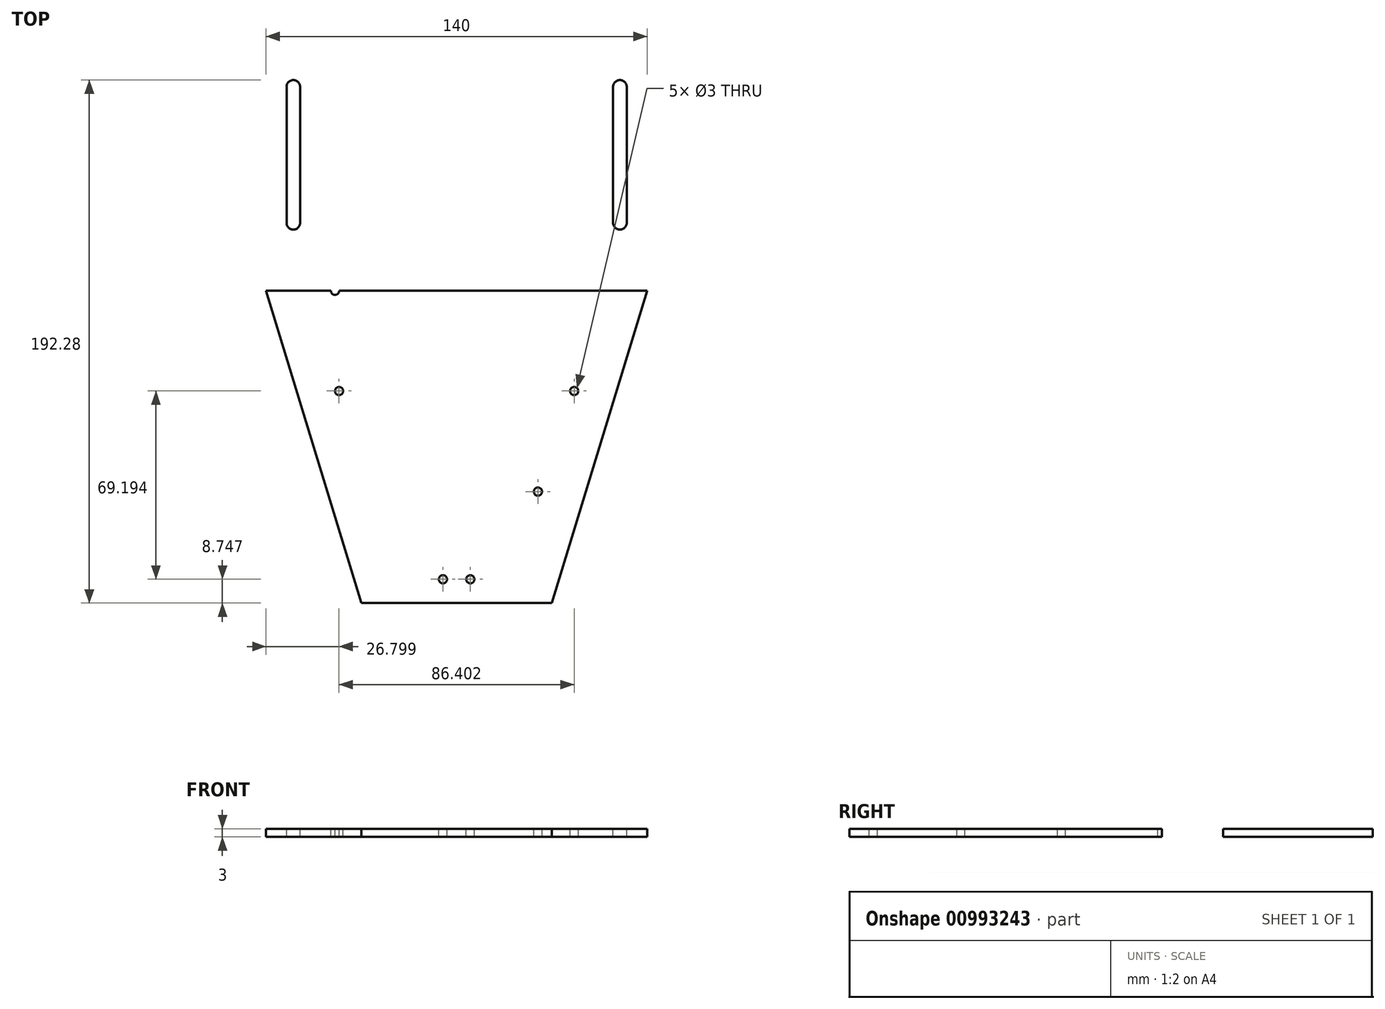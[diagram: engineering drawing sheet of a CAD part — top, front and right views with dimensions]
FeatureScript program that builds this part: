
annotation { "Feature Type Name" : "Feature", "Feature Type Description" : "" }
export const myFeature = defineFeature(function(context is Context, id is Id, definition is map)
    precondition{}
    {
        {
            var Q0;
            Q0=qCreatedBy(makeId("Top.planeOp"),FACE);
            var sketch = newSketch(context, id + "F0", { "sketchPlane" : qUnion([Q0])});
            skLineSegment(sketch, "E0.bottom", {"start": v(0, 0) * mm, "end": v(70, 0) * mm});
            skLineSegment(sketch, "E0.top", {"start": v(0, 80) * mm, "end": v(70, 80) * mm});
            skLineSegment(sketch, "E0.left", {"start": v(0, 0) * mm, "end": v(0, 80) * mm});
            skLineSegment(sketch, "E0.right", {"start": v(70, 0) * mm, "end": v(70, 80) * mm});
            skSolve(sketch);
        }
        {
            var Q0;
            Q0=makeQuery(id+"F0.imprint","IMPRINT",FACE,{"disambiguationData":[TD([[makeQuery(id+"F0.imprint","IMPRINT",EDGE,{"derivedFrom":sQuery(id+"F0.wireOp",EDGE,"E0.bottom")}),1.0]])]});
            extrude(context, id + "F1", {"entities" : qUnion([Q0]), "depth" : 3 * mm, "offsetDistance" : 25 * mm});
        }
        {
            var Q0;
            Q0=makeQuery(id+"F1.opExtrude","CAP_FACE",FACE,{"disambiguationData":[OSD([sQuery(id+"F0.wireOp",EDGE,"E0.bottom"),sQuery(id+"F0.wireOp",EDGE,"E0.top"),sQuery(id+"F0.wireOp",EDGE,"E0.left"),sQuery(id+"F0.wireOp",EDGE,"E0.right")])],"isStart":false});
            var sketch = newSketch(context, id + "F2", { "sketchPlane" : qUnion([Q0])});
            skLineSegment(sketch, "E1", {"start": v(45, 61) * mm, "end": v(45, 37) * mm});
            skLineSegment(sketch, "E2", {"start": v(0, 12) * mm, "end": v(0, -12) * mm});
            skSolve(sketch);
        }
        {
            var Q0;
            Q0=sQuery(id+"F2.wireOp",VERTEX,"E1.start");
            var Q1;
            Q1=sQuery(id+"F2.wireOp",VERTEX,"E1.end");
            var Q2;
            Q2=makeQuery(id+"F1.opExtrude","SWEPT_BODY",BODY,{"disambiguationData":[OSD([sQuery(id+"F0.wireOp",EDGE,"E0.bottom"),sQuery(id+"F0.wireOp",EDGE,"E0.top"),sQuery(id+"F0.wireOp",EDGE,"E0.left"),sQuery(id+"F0.wireOp",EDGE,"E0.right")])]});
            hole(context, id + "F3", {"style" : HoleStyle.SIMPLE, "endStyle" : HoleEndStyle.THROUGH, "holeDiameter" : 3 * mm, "majorDiameter" : 5 * mm, "isTappedThrough" : true, "tappedDepth" : 12 * mm, "tapClearance" : 3, "locations" : qUnion([Q0, Q1]), "scope" : qUnion([Q2])});
        }
        {
            var Q0;
            Q0=makeQuery(id+"F1.opExtrude","CAP_FACE",FACE,{"disambiguationData":[OSD([sQuery(id+"F0.wireOp",EDGE,"E0.bottom"),sQuery(id+"F0.wireOp",EDGE,"E0.top"),sQuery(id+"F0.wireOp",EDGE,"E0.left"),sQuery(id+"F0.wireOp",EDGE,"E0.right")])],"isStart":false});
            var sketch = newSketch(context, id + "F4", { "sketchPlane" : qUnion([Q0])});
            skLineSegment(sketch, "E3", {"start": v(60, 75) * mm, "end": v(60, 25) * mm});
            skSolve(sketch);
        }
        {
            var Q0;
            Q0=makeQuery(id+"F4.imprint","IMPRINT",FACE,{"disambiguationData":[TD([[makeQuery(id+"F4.imprint","IMPRINT",EDGE,{"derivedFrom":makeQuery(id+"F1.opExtrude","CAP_EDGE",EDGE,{"disambiguationData":[OSD([sQuery(id+"F0.wireOp",EDGE,"E0.bottom")])],"isStart":false})}),1.0]])]});
            var sketch = newSketch(context, id + "F5", { "sketchPlane" : qUnion([Q0])});
            skLineSegment(sketch, "E4.JUB.JUB", {"start": v(60, 75) * mm, "end": v(60, 25) * mm, "construction": true});
            skArc(sketch, "E4.0.startCap", {"start": v(57.5, 75) * mm, "mid": v(60, 77.5) * mm, "end": v(62.5, 75) * mm});
            skArc(sketch, "E4.0.endCap", {"start": v(62.5, 25) * mm, "mid": v(60, 22.5) * mm, "end": v(57.5, 25) * mm});
            skLineSegment(sketch, "E4.0.left", {"start": v(62.5, 75) * mm, "end": v(62.5, 25) * mm});
            skLineSegment(sketch, "E4.0.right", {"start": v(57.5, 75) * mm, "end": v(57.5, 25) * mm});
            skSolve(sketch);
        }
        {
            var Q0;
            Q0=makeQuery(id+"F1.opExtrude","CAP_FACE",FACE,{"disambiguationData":[OSD([sQuery(id+"F0.wireOp",EDGE,"E0.bottom"),sQuery(id+"F0.wireOp",EDGE,"E0.top"),sQuery(id+"F0.wireOp",EDGE,"E0.left"),sQuery(id+"F0.wireOp",EDGE,"E0.right")])],"isStart":false});
            var sketch = newSketch(context, id + "F6", { "sketchPlane" : qUnion([Q0])});
            skLineSegment(sketch, "E5", {"start": v(70, 0) * mm, "end": v(35, -114.78) * mm});
            skPoint(sketch, "E5.endSnap0", {"position": v(35, 0) * mm});
            skLineSegment(sketch, "E6", {"start": v(35, -114.78) * mm, "end": v(0, -114.78) * mm});
            skLineSegment(sketch, "E7", {"start": v(0, -114.78) * mm, "end": v(0, 0) * mm});
            skSolve(sketch);
        }
        {
            var Q0;
            Q0=makeQuery(id+"F6.imprint","IMPRINT",FACE,{"disambiguationData":[TD([[makeQuery(id+"F6.imprint","IMPRINT",EDGE,{"derivedFrom":sQuery(id+"F6.wireOp",EDGE,"E5")}),-1.0]])]});
            extrude(context, id + "F7", {"entities" : qUnion([Q0]), "operationType" : NewBodyOperationType.ADD, "oppositeDirection" : true, "depth" : 3 * mm, "offsetDistance" : 25 * mm});
        }
        {
            var Q0;
            {var subQ0=sQuery(id+"F0.wireOp",EDGE,"E0.bottom");var subQ1=makeQuery(id+"F7.boolean.opBoolean","MERGE",FACE,{"derivedFrom":[makeQuery(id+"F1.opExtrude","CAP_FACE",FACE,{"disambiguationData":[OSD([subQ0,sQuery(id+"F0.wireOp",EDGE,"E0.top"),sQuery(id+"F0.wireOp",EDGE,"E0.left"),sQuery(id+"F0.wireOp",EDGE,"E0.right")])],"isStart":false}),makeQuery(id+"F7.opExtrude","CAP_FACE",FACE,{"disambiguationData":[OSD([subQ0,sQuery(id+"F6.wireOp",EDGE,"E5"),sQuery(id+"F6.wireOp",EDGE,"E6"),sQuery(id+"F6.wireOp",EDGE,"E7")])],"isStart":true})]});Q0=makeQuery(id+"FWdn2cQ6DDmUmaq_1.boolean.opBoolean","MERGE",FACE,{"derivedFrom":[subQ1,makeQuery(id+"FWdn2cQ6DDmUmaq_1.opPattern","COPY",FACE,{"derivedFrom":subQ1,"instanceName":"1"})]});}
            var sketch = newSketch(context, id + "F8", { "sketchPlane" : qUnion([Q0])});
            skLineSegment(sketch, "E8", {"start": v(-41.8, -36.84) * mm, "end": v(43.2, -36.84) * mm});
            skSolve(sketch);
        }
        {
            var Q0;
            Q0=sQuery(id+"F8.wireOp",VERTEX,"E8.start");
            var Q1;
            Q1=sQuery(id+"F8.wireOp",VERTEX,"E8.end");
            var Q2;
            Q2=makeQuery(id+"F1.opExtrude","SWEPT_BODY",BODY,{"disambiguationData":[OSD([sQuery(id+"F0.wireOp",EDGE,"E0.bottom"),sQuery(id+"F0.wireOp",EDGE,"E0.top"),sQuery(id+"F0.wireOp",EDGE,"E0.left"),sQuery(id+"F0.wireOp",EDGE,"E0.right")])]});
            hole(context, id + "F9", {"style" : HoleStyle.SIMPLE, "endStyle" : HoleEndStyle.THROUGH, "holeDiameter" : 3 * mm, "majorDiameter" : 5 * mm, "isTappedThrough" : true, "tappedDepth" : 12 * mm, "tapClearance" : 3, "locations" : qUnion([Q0, Q1]), "scope" : qUnion([Q2])});
        }
        {
            var Q0;
            {var subQ0=sQuery(id+"F0.wireOp",EDGE,"E0.bottom");var subQ1=makeQuery(id+"F7.boolean.opBoolean","MERGE",FACE,{"derivedFrom":[makeQuery(id+"F1.opExtrude","CAP_FACE",FACE,{"disambiguationData":[OSD([subQ0,sQuery(id+"F0.wireOp",EDGE,"E0.top"),sQuery(id+"F0.wireOp",EDGE,"E0.left"),sQuery(id+"F0.wireOp",EDGE,"E0.right")])],"isStart":false}),makeQuery(id+"F7.opExtrude","CAP_FACE",FACE,{"disambiguationData":[OSD([subQ0,sQuery(id+"F6.wireOp",EDGE,"E5"),sQuery(id+"F6.wireOp",EDGE,"E6"),sQuery(id+"F6.wireOp",EDGE,"E7")])],"isStart":true})]});Q0=makeQuery(id+"FWdn2cQ6DDmUmaq_1.boolean.opBoolean","MERGE",FACE,{"derivedFrom":[subQ1,makeQuery(id+"FWdn2cQ6DDmUmaq_1.opPattern","COPY",FACE,{"derivedFrom":subQ1,"instanceName":"1"})]});}
            var sketch = newSketch(context, id + "F10", { "sketchPlane" : qUnion([Q0])});
            skLineSegment(sketch, "E9", {"start": v(-13.97, -106.03) * mm, "end": v(5.03, -106.03) * mm});
            skSolve(sketch);
        }
        {
            var Q0;
            Q0=sQuery(id+"F10.wireOp",VERTEX,"E9.start");
            var Q1;
            Q1=sQuery(id+"F10.wireOp",VERTEX,"E9.end");
            var Q2;
            Q2=makeQuery(id+"F1.opExtrude","SWEPT_BODY",BODY,{"disambiguationData":[OSD([sQuery(id+"F0.wireOp",EDGE,"E0.bottom"),sQuery(id+"F0.wireOp",EDGE,"E0.top"),sQuery(id+"F0.wireOp",EDGE,"E0.left"),sQuery(id+"F0.wireOp",EDGE,"E0.right")])]});
            hole(context, id + "F11", {"style" : HoleStyle.SIMPLE, "endStyle" : HoleEndStyle.THROUGH, "holeDiameter" : 3 * mm, "majorDiameter" : 5 * mm, "isTappedThrough" : true, "tappedDepth" : 12 * mm, "tapClearance" : 3, "locations" : qUnion([Q0, Q1]), "scope" : qUnion([Q2])});
        }
        {
            var Q0;
            Q0=makeQuery(id+"F5.imprint","IMPRINT",FACE,{"disambiguationData":[TD([[makeQuery(id+"F5.imprint","IMPRINT",EDGE,{"derivedFrom":sQuery(id+"F5.wireOp",EDGE,"E4.0.startCap")}),-1.0]])]});
            extrude(context, id + "F12", {"entities" : qUnion([Q0]), "operationType" : NewBodyOperationType.REMOVE, "oppositeDirection" : true, "depth" : 25 * mm, "offsetDistance" : 25 * mm});
        }
        {
            var Q0;
            {var subQ0=sQuery(id+"F0.wireOp",EDGE,"E0.bottom");var subQ1=makeQuery(id+"F7.boolean.opBoolean","MERGE",FACE,{"derivedFrom":[makeQuery(id+"F1.opExtrude","CAP_FACE",FACE,{"disambiguationData":[OSD([subQ0,sQuery(id+"F0.wireOp",EDGE,"E0.top"),sQuery(id+"F0.wireOp",EDGE,"E0.left"),sQuery(id+"F0.wireOp",EDGE,"E0.right")])],"isStart":false}),makeQuery(id+"F7.opExtrude","CAP_FACE",FACE,{"disambiguationData":[OSD([subQ0,sQuery(id+"F6.wireOp",EDGE,"E5"),sQuery(id+"F6.wireOp",EDGE,"E6"),sQuery(id+"F6.wireOp",EDGE,"E7")])],"isStart":true})]});Q0=makeQuery(id+"FWdn2cQ6DDmUmaq_1.boolean.opBoolean","MERGE",FACE,{"derivedFrom":[subQ1,makeQuery(id+"FWdn2cQ6DDmUmaq_1.opPattern","COPY",FACE,{"derivedFrom":subQ1,"instanceName":"1"})]});}
            var sketch = newSketch(context, id + "F13", { "sketchPlane" : qUnion([Q0])});
            skLineSegment(sketch, "E10", {"start": v(-35.13, -73.83) * mm, "end": v(29.87, -73.83) * mm});
            skSolve(sketch);
        }
        {
            var Q0;
            Q0=makeQuery(id+"F1.opExtrude","SWEPT_BODY",BODY,{"disambiguationData":[OSD([sQuery(id+"F0.wireOp",EDGE,"E0.bottom"),sQuery(id+"F0.wireOp",EDGE,"E0.top"),sQuery(id+"F0.wireOp",EDGE,"E0.left"),sQuery(id+"F0.wireOp",EDGE,"E0.right")])]});
            var Q1;
            Q1=qCreatedBy(makeId("Right.planeOp"),FACE);
            mirror(context, id + "F14", {"operationType" : NewBodyOperationType.ADD, "entities" : qUnion([Q0]), "mirrorPlane" : qUnion([Q1])});
        }
        {
            var Q0;
            Q0=sQuery(id+"F13.wireOp",VERTEX,"E10.end");
            var Q1;
            Q1=makeQuery(id+"F1.opExtrude","SWEPT_BODY",BODY,{"disambiguationData":[OSD([sQuery(id+"F0.wireOp",EDGE,"E0.bottom"),sQuery(id+"F0.wireOp",EDGE,"E0.top"),sQuery(id+"F0.wireOp",EDGE,"E0.left"),sQuery(id+"F0.wireOp",EDGE,"E0.right")])]});
            hole(context, id + "F15", {"style" : HoleStyle.SIMPLE, "endStyle" : HoleEndStyle.THROUGH, "holeDiameter" : 3 * mm, "majorDiameter" : 5 * mm, "isTappedThrough" : true, "tappedDepth" : 12 * mm, "tapClearance" : 3, "locations" : qUnion([Q0]), "scope" : qUnion([Q1])});
        }
        {
            var Q0;
            {var subQ0=sQuery(id+"F0.wireOp",EDGE,"E0.bottom");var subQ1=makeQuery(id+"F7.boolean.opBoolean","MERGE",FACE,{"derivedFrom":[makeQuery(id+"F1.opExtrude","CAP_FACE",FACE,{"disambiguationData":[OSD([subQ0,sQuery(id+"F0.wireOp",EDGE,"E0.top"),sQuery(id+"F0.wireOp",EDGE,"E0.left"),sQuery(id+"F0.wireOp",EDGE,"E0.right")])],"isStart":false}),makeQuery(id+"F7.opExtrude","CAP_FACE",FACE,{"disambiguationData":[OSD([subQ0,sQuery(id+"F6.wireOp",EDGE,"E5"),sQuery(id+"F6.wireOp",EDGE,"E6"),sQuery(id+"F6.wireOp",EDGE,"E7")])],"isStart":true})]});Q0=makeQuery(id+"F14.boolean.opBoolean","MERGE",FACE,{"derivedFrom":[subQ1,makeQuery(id+"F14.opPattern","COPY",FACE,{"derivedFrom":subQ1,"instanceName":"1"})]});}
            var sketch = newSketch(context, id + "F16", { "sketchPlane" : qUnion([Q0])});
            skLineSegment(sketch, "E11", {"start": v(0, 0) * mm, "end": v(-44.68, 0) * mm});
            skSolve(sketch);
        }
        {
            var Q0;
            Q0=sQuery(id+"F16.wireOp",VERTEX,"E11.end");
            var Q1;
            Q1=makeQuery(id+"F1.opExtrude","SWEPT_BODY",BODY,{"disambiguationData":[OSD([sQuery(id+"F0.wireOp",EDGE,"E0.bottom"),sQuery(id+"F0.wireOp",EDGE,"E0.top"),sQuery(id+"F0.wireOp",EDGE,"E0.left"),sQuery(id+"F0.wireOp",EDGE,"E0.right")])]});
            hole(context, id + "F17", {"style" : HoleStyle.SIMPLE, "endStyle" : HoleEndStyle.THROUGH, "holeDiameter" : 3 * mm, "majorDiameter" : 5 * mm, "isTappedThrough" : true, "tappedDepth" : 12 * mm, "tapClearance" : 3, "locations" : qUnion([Q0]), "scope" : qUnion([Q1])});
        }
    });
